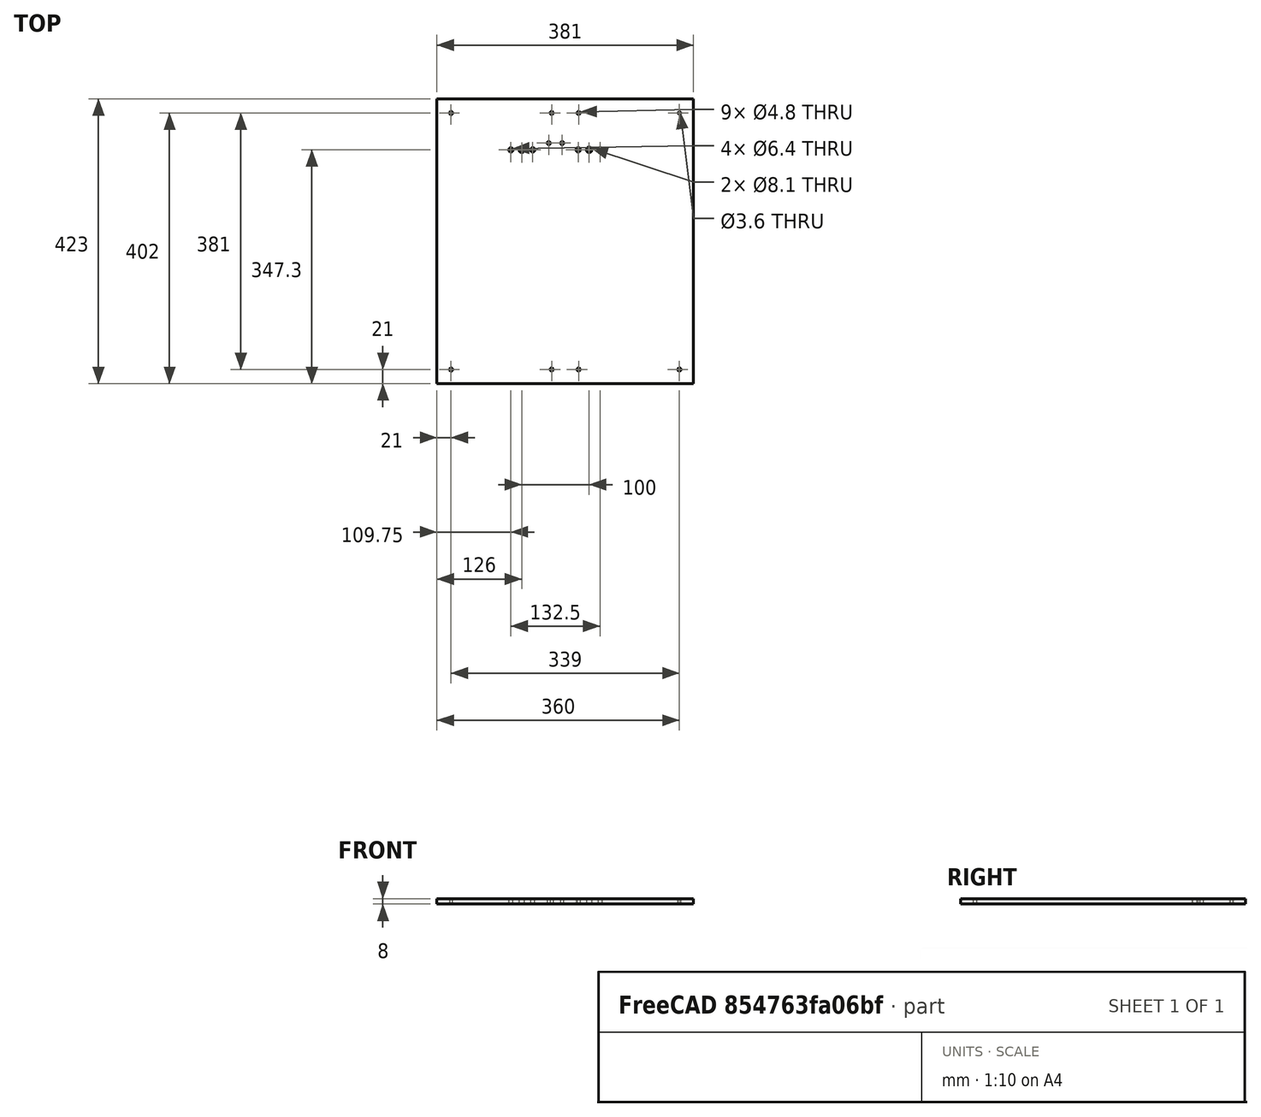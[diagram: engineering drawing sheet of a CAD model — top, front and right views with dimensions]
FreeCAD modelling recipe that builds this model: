
FCSTD DOCUMENT  (FreeCAD 0.16R6706 (Git))
Label: Piso
License: All rights reserved
LicenseURL: http://en.wikipedia.org/wiki/All_rights_reserved
objects: Path::FeaturePython×19, Sketcher::SketchObject×1, PartDesign::Pad×1, Path::FeatureCompoundPython×1
note: 3 computed .brp shape members not serialized (recipe doc carries the construction recipe); baked Part::Feature solids carry a one-line shape summary decoded from their .brp

FEATURE [Sketcher::SketchObject] Sketch
  sketch-geometry (29):
    g0: LineSegment StartX=-381 StartY=423 StartZ=0 EndX=0 EndY=423 EndZ=0
    g1: LineSegment StartX=0 StartY=423 StartZ=0 EndX=0 EndY=0 EndZ=0
    g2: LineSegment StartX=0 StartY=0 StartZ=0 EndX=-381 EndY=0 EndZ=0
    g3: LineSegment StartX=-381 StartY=0 StartZ=0 EndX=-381 EndY=423 EndZ=0
    g4: Circle CenterX=-360 CenterY=402 CenterZ=0 NormalX=0 NormalY=0 NormalZ=1 Radius=2.4
    g5: Circle CenterX=-21 CenterY=402 CenterZ=0 NormalX=0 NormalY=0 NormalZ=1 Radius=1.8
    g6: LineSegment [constr] StartX=-360 StartY=402 StartZ=0 EndX=-21 EndY=402 EndZ=0
    g7: LineSegment [constr] StartX=-21 StartY=402 StartZ=0 EndX=-21 EndY=21 EndZ=0
    g8: LineSegment [constr] StartX=-21 StartY=21 StartZ=0 EndX=-360 EndY=21 EndZ=0
    g9: LineSegment [constr] StartX=-360 StartY=21 StartZ=0 EndX=-360 EndY=402 EndZ=0
    g10: Circle CenterX=-360 CenterY=21 CenterZ=0 NormalX=0 NormalY=0 NormalZ=1 Radius=2.4
    g11: Circle CenterX=-21 CenterY=21 CenterZ=0 NormalX=0 NormalY=0 NormalZ=1 Radius=2.4
    g12: LineSegment [constr] StartX=-171.25 StartY=347.3 StartZ=0 EndX=-138.75 EndY=347.3 EndZ=0
    g13: Circle CenterX=-171.25 CenterY=347.3 CenterZ=0 NormalX=0 NormalY=0 NormalZ=1 Radius=3.2
    g14: Circle CenterX=-138.75 CenterY=347.3 CenterZ=0 NormalX=0 NormalY=0 NormalZ=1 Radius=3.2
    g15: LineSegment [constr] StartX=-271.25 StartY=347.3 StartZ=0 EndX=-238.75 EndY=347.3 EndZ=0
    g16: Circle CenterX=-271.25 CenterY=347.3 CenterZ=0 NormalX=0 NormalY=0 NormalZ=1 Radius=3.2
    g17: Circle CenterX=-238.75 CenterY=347.3 CenterZ=0 NormalX=0 NormalY=0 NormalZ=1 Radius=3.2
    g18: LineSegment [constr] StartX=-255 StartY=347.3 StartZ=0 EndX=-155 EndY=347.3 EndZ=0
    g19: LineSegment [constr] StartX=-205 StartY=347.3 StartZ=0 EndX=-205 EndY=327.3 EndZ=0
    g20: LineSegment [constr] StartX=-215 StartY=357.3 StartZ=0 EndX=-195 EndY=357.3 EndZ=0
    g21: Circle CenterX=-215 CenterY=357.3 CenterZ=0 NormalX=0 NormalY=0 NormalZ=1 Radius=2.4
    g22: Circle CenterX=-195 CenterY=357.3 CenterZ=0 NormalX=0 NormalY=0 NormalZ=1 Radius=2.4
    g23: Circle CenterX=-210.5 CenterY=402 CenterZ=0 NormalX=0 NormalY=0 NormalZ=1 Radius=2.4
    g24: Circle CenterX=-170.5 CenterY=402 CenterZ=0 NormalX=0 NormalY=0 NormalZ=1 Radius=2.4
    g25: Circle CenterX=-210.5 CenterY=21 CenterZ=0 NormalX=0 NormalY=0 NormalZ=1 Radius=2.4
    g26: Circle CenterX=-170.5 CenterY=21 CenterZ=0 NormalX=0 NormalY=0 NormalZ=1 Radius=2.4
    g27: Circle CenterX=-255 CenterY=347.3 CenterZ=0 NormalX=0 NormalY=0 NormalZ=1 Radius=4.05
    g28: Circle CenterX=-155 CenterY=347.3 CenterZ=0 NormalX=0 NormalY=0 NormalZ=1 Radius=4.05
  constraints (76):
    c: Coincident(g0,g1)
    c: Coincident(g1,g2)
    c: Coincident(g2,g3)
    c: Coincident(g3,g0)
    c: Horizontal(g0)
    c: Horizontal(g2)
    c: Vertical(g1)
    c: Vertical(g3)
    c: DistanceX(g0,g0) = 381
    c: DistanceY(g1,g1) = 423
    c: Coincident(g-1,g1)
    c: Radius(g4) = 2.4
    c: Coincident(g6,g7)
    c: Coincident(g7,g8)
    c: Coincident(g8,g9)
    c: Coincident(g9,g6)
    c: Horizontal(g6)
    c: Horizontal(g8)
    c: Vertical(g7)
    c: Vertical(g9)
    c: DistanceY(g-1,g7) = 21
    c: DistanceX(g7,g-1) = 21
    c: DistanceX(g0,g6) = 21
    c: DistanceY(g6,g0) = 21
    c: Equal(g4,g10) = 1.8
    c: Equal(g4,g11) = 1.8
    c: Coincident(g4,g6)
    c: Coincident(g5,g6)
    c: Coincident(g7,g11)
    c: Coincident(g8,g10)
    c: DistanceX(g12,g12) = 32.5
    c: Horizontal(g12)
    c: Radius(g13) = 3.2
    c: Equal(g13,g14) = 3.2
    c: Coincident(g12,g14)
    c: Coincident(g12,g13)
    c: Equal(g12,g15) = 32.5
    c: Horizontal(g15)
    c: Equal(g13,g16) = 3.2
    c: Equal(g16,g17) = 3.2
    c: Coincident(g15,g17)
    c: Coincident(g15,g16)
    c: DistanceX(g18,g18) = 100
    c: DistanceY(g19,g19) = 20
    c: Symmetric(g18,g18,g19)
    c: Horizontal(g18)
    c: Vertical(g19)
    c: Symmetric(g15,g15,g18)
    c: Symmetric(g12,g12,g18)
    c: DistanceX(g19,g0) = 205
    c: Horizontal(g20)
    c: DistanceX(g20,g20) = 20
    c: DistanceY(g19,g20) = 30
    c: Symmetric(g20,g20,g19)
    c: Equal(g4,g21) = 1.8
    c: Equal(g4,g22) = 1.8
    c: Coincident(g20,g21)
    c: Coincident(g22,g20)
    c: DistanceY(g12,g0) = 75.7
    c: DistanceX(g6,g6) = 339
    c: Radius(g23) = 2.4
    c: PointOnObject(g23,g6)
    c: DistanceX(g4,g23) = 149.5
    c: Equal(g23,g24) = 2.4
    c: PointOnObject(g24,g6)
    c: DistanceX(g23,g24) = 40
    c: Equal(g23,g25) = 2.4
    c: PointOnObject(g25,g8)
    c: DistanceX(g8,g25) = 149.5
    c: Equal(g23,g26) = 2.4
    c: PointOnObject(g26,g8)
    c: DistanceX(g25,g26) = 40
    c: Radius(g27) = 4.05
    c: Equal(g27,g28) = 4.05
    c: Coincident(g18,g28)
    c: Coincident(g18,g27)
FEATURE [PartDesign::Pad] Pad
  Length = 8
  Length2 = 100
  Sketch = -> Sketch
  Type = 0
FEATURE [Path::FeaturePython] Machine  label="Machine_"  # Path/CAM operation (typed FeaturePython)
  MachineUnits = 0
  X = 0
  X_Max = 0
  X_Min = 0
  Y = 0
  Y_Max = 0
  Y_Min = 0
  Z = 0
  Z_Max = 0
  Z_Min = 0
FEATURE [Path::FeaturePython] Tool  label="Tool1"  # Path/CAM operation (typed FeaturePython)
  SpindleDir = 0
  SpindleSpeed = 0
  ToolNumber = 1
FEATURE [Path::FeaturePython] Profile  label="Cantoneira"  # Path/CAM operation (typed FeaturePython)
  Active = true
  Base = -> Sketch
  ClearanceHeight = 3
  Direction = 1
  Edge1 = -> Sketch [Edge5]
  EndPoint = (0,0,0)
  ExtendAtEnd = 0
  ExtendAtStart = 0
  FinalDepth = -15.2
  HorizFeed = 127
  LeadInLineLen = 0
  LeadOutLineLen = 0
  OffsetExtra = 0
  PathClosed = true
  RetractHeight = 0
  RollRadius = 0
  SegLen = 0.5
  Side = 1
  StartDepth = 0
  StartPoint = (0,0,0)
  StepDown = 3
  ToolNumber = 1
  UseEndPoint = false
  UsePlacements = false
  UseStartDepth = true
  UseStartPoint = false
  VertFeed = 127
FEATURE [Path::FeaturePython] Profile001  label="Cantoneira001"  # Path/CAM operation (typed FeaturePython)
  Active = true
  Base = -> Sketch
  ClearanceHeight = 3
  Direction = 1
  Edge1 = -> Sketch [Edge15]
  EndPoint = (0,0,0)
  ExtendAtEnd = 0
  ExtendAtStart = 0
  FinalDepth = -15.2
  HorizFeed = 127
  LeadInLineLen = 0
  LeadOutLineLen = 0
  OffsetExtra = 0
  PathClosed = true
  RetractHeight = 0
  RollRadius = 0
  SegLen = 0.5
  Side = 1
  StartDepth = 0
  StartPoint = (0,0,0)
  StepDown = 3
  ToolNumber = 1
  UseEndPoint = false
  UsePlacements = false
  UseStartDepth = true
  UseStartPoint = false
  VertFeed = 127
FEATURE [Path::FeaturePython] Profile002  label="Cantoneira002"  # Path/CAM operation (typed FeaturePython)
  Active = true
  Base = -> Sketch
  ClearanceHeight = 3
  Direction = 1
  Edge1 = -> Sketch [Edge16]
  EndPoint = (0,0,0)
  ExtendAtEnd = 0
  ExtendAtStart = 0
  FinalDepth = -15.2
  HorizFeed = 127
  LeadInLineLen = 0
  LeadOutLineLen = 0
  OffsetExtra = 0
  PathClosed = true
  RetractHeight = 0
  RollRadius = 0
  SegLen = 0.5
  Side = 1
  StartDepth = 0
  StartPoint = (0,0,0)
  StepDown = 3
  ToolNumber = 1
  UseEndPoint = false
  UsePlacements = false
  UseStartDepth = true
  UseStartPoint = false
  VertFeed = 127
FEATURE [Path::FeaturePython] Profile003  label="Cantoneira003"  # Path/CAM operation (typed FeaturePython)
  Active = true
  Base = -> Sketch
  ClearanceHeight = 3
  Direction = 1
  Edge1 = -> Sketch [Edge6]
  EndPoint = (0,0,0)
  ExtendAtEnd = 0
  ExtendAtStart = 0
  FinalDepth = -15.2
  HorizFeed = 127
  LeadInLineLen = 0
  LeadOutLineLen = 0
  OffsetExtra = 0
  PathClosed = true
  RetractHeight = 0
  RollRadius = 0
  SegLen = 0.5
  Side = 1
  StartDepth = 0
  StartPoint = (0,0,0)
  StepDown = 3
  ToolNumber = 1
  UseEndPoint = false
  UsePlacements = false
  UseStartDepth = true
  UseStartPoint = false
  VertFeed = 127
FEATURE [Path::FeaturePython] Profile004  label="Cantoneira004"  # Path/CAM operation (typed FeaturePython)
  Active = true
  Base = -> Sketch
  ClearanceHeight = 3
  Direction = 1
  Edge1 = -> Sketch [Edge7]
  EndPoint = (0,0,0)
  ExtendAtEnd = 0
  ExtendAtStart = 0
  FinalDepth = -15.2
  HorizFeed = 127
  LeadInLineLen = 0
  LeadOutLineLen = 0
  OffsetExtra = 0
  PathClosed = true
  RetractHeight = 0
  RollRadius = 0
  SegLen = 0.5
  Side = 1
  StartDepth = 0
  StartPoint = (0,0,0)
  StepDown = 3
  ToolNumber = 1
  UseEndPoint = false
  UsePlacements = false
  UseStartDepth = true
  UseStartPoint = false
  VertFeed = 127
FEATURE [Path::FeaturePython] Profile005  label="Cantoneira005"  # Path/CAM operation (typed FeaturePython)
  Active = true
  Base = -> Sketch
  ClearanceHeight = 3
  Direction = 1
  Edge1 = -> Sketch [Edge17]
  EndPoint = (0,0,0)
  ExtendAtEnd = 0
  ExtendAtStart = 0
  FinalDepth = -15.2
  HorizFeed = 127
  LeadInLineLen = 0
  LeadOutLineLen = 0
  OffsetExtra = 0
  PathClosed = true
  RetractHeight = 0
  RollRadius = 0
  SegLen = 0.5
  Side = 1
  StartDepth = 0
  StartPoint = (0,0,0)
  StepDown = 3
  ToolNumber = 1
  UseEndPoint = false
  UsePlacements = false
  UseStartDepth = true
  UseStartPoint = false
  VertFeed = 127
FEATURE [Path::FeaturePython] Profile006  label="Cantoneira006"  # Path/CAM operation (typed FeaturePython)
  Active = true
  Base = -> Sketch
  ClearanceHeight = 3
  Direction = 1
  Edge1 = -> Sketch [Edge18]
  EndPoint = (0,0,0)
  ExtendAtEnd = 0
  ExtendAtStart = 0
  FinalDepth = -15.2
  HorizFeed = 127
  LeadInLineLen = 0
  LeadOutLineLen = 0
  OffsetExtra = 0
  PathClosed = true
  RetractHeight = 0
  RollRadius = 0
  SegLen = 0.5
  Side = 1
  StartDepth = 0
  StartPoint = (0,0,0)
  StepDown = 3
  ToolNumber = 1
  UseEndPoint = false
  UsePlacements = false
  UseStartDepth = true
  UseStartPoint = false
  VertFeed = 127
FEATURE [Path::FeaturePython] Profile007  label="Cantoneira007"  # Path/CAM operation (typed FeaturePython)
  Active = true
  Base = -> Sketch
  ClearanceHeight = 3
  Direction = 1
  Edge1 = -> Sketch [Edge8]
  EndPoint = (0,0,0)
  ExtendAtEnd = 0
  ExtendAtStart = 0
  FinalDepth = -15.2
  HorizFeed = 127
  LeadInLineLen = 0
  LeadOutLineLen = 0
  OffsetExtra = 0
  PathClosed = true
  RetractHeight = 0
  RollRadius = 0
  SegLen = 0.5
  Side = 1
  StartDepth = 0
  StartPoint = (0,0,0)
  StepDown = 3
  ToolNumber = 1
  UseEndPoint = false
  UsePlacements = false
  UseStartDepth = true
  UseStartPoint = false
  VertFeed = 127
FEATURE [Path::FeaturePython] Profile008  label="Motor e Haste"  # Path/CAM operation (typed FeaturePython)
  Active = true
  Base = -> Sketch
  ClearanceHeight = 3
  Direction = 1
  Edge1 = -> Sketch [Edge11]
  EndPoint = (0,0,0)
  ExtendAtEnd = 0
  ExtendAtStart = 0
  FinalDepth = -15.2
  HorizFeed = 127
  LeadInLineLen = 0
  LeadOutLineLen = 0
  OffsetExtra = 0
  PathClosed = true
  RetractHeight = 0
  RollRadius = 0
  SegLen = 0.5
  Side = 1
  StartDepth = 0
  StartPoint = (0,0,0)
  StepDown = 3
  ToolNumber = 1
  UseEndPoint = false
  UsePlacements = false
  UseStartDepth = true
  UseStartPoint = false
  VertFeed = 127
FEATURE [Path::FeaturePython] Profile009  label="Motor e Haste001"  # Path/CAM operation (typed FeaturePython)
  Active = true
  Base = -> Sketch
  ClearanceHeight = 3
  Direction = 1
  Edge1 = -> Sketch [Edge19]
  EndPoint = (0,0,0)
  ExtendAtEnd = 0
  ExtendAtStart = 0
  FinalDepth = -15.2
  HorizFeed = 127
  LeadInLineLen = 0
  LeadOutLineLen = 0
  OffsetExtra = 0
  PathClosed = true
  RetractHeight = 0
  RollRadius = 0
  SegLen = 0.5
  Side = 1
  StartDepth = 0
  StartPoint = (0,0,0)
  StepDown = 3
  ToolNumber = 1
  UseEndPoint = false
  UsePlacements = false
  UseStartDepth = true
  UseStartPoint = false
  VertFeed = 127
FEATURE [Path::FeaturePython] Profile010  label="Motor e Haste002"  # Path/CAM operation (typed FeaturePython)
  Active = true
  Base = -> Sketch
  ClearanceHeight = 3
  Direction = 1
  Edge1 = -> Sketch [Edge12]
  EndPoint = (0,0,0)
  ExtendAtEnd = 0
  ExtendAtStart = 0
  FinalDepth = -15.2
  HorizFeed = 127
  LeadInLineLen = 0
  LeadOutLineLen = 0
  OffsetExtra = 0
  PathClosed = true
  RetractHeight = 0
  RollRadius = 0
  SegLen = 0.5
  Side = 1
  StartDepth = 0
  StartPoint = (0,0,0)
  StepDown = 3
  ToolNumber = 1
  UseEndPoint = false
  UsePlacements = false
  UseStartDepth = true
  UseStartPoint = false
  VertFeed = 127
FEATURE [Path::FeaturePython] Profile011  label="Motor e Haste003"  # Path/CAM operation (typed FeaturePython)
  Active = true
  Base = -> Sketch
  ClearanceHeight = 3
  Direction = 1
  Edge1 = -> Sketch [Edge13]
  EndPoint = (0,0,0)
  ExtendAtEnd = 0
  ExtendAtStart = 0
  FinalDepth = -15.2
  HorizFeed = 127
  LeadInLineLen = 0
  LeadOutLineLen = 0
  OffsetExtra = 0
  PathClosed = true
  RetractHeight = 0
  RollRadius = 0
  SegLen = 0.5
  Side = 1
  StartDepth = 0
  StartPoint = (0,0,0)
  StepDown = 3
  ToolNumber = 1
  UseEndPoint = false
  UsePlacements = false
  UseStartDepth = true
  UseStartPoint = false
  VertFeed = 127
FEATURE [Path::FeaturePython] Profile012  label="Motor e Haste004"  # Path/CAM operation (typed FeaturePython)
  Active = true
  Base = -> Sketch
  ClearanceHeight = 3
  Direction = 1
  Edge1 = -> Sketch [Edge14]
  EndPoint = (0,0,0)
  ExtendAtEnd = 0
  ExtendAtStart = 0
  FinalDepth = -15.2
  HorizFeed = 127
  LeadInLineLen = 0
  LeadOutLineLen = 0
  OffsetExtra = 0
  PathClosed = true
  RetractHeight = 0
  RollRadius = 0
  SegLen = 0.5
  Side = 1
  StartDepth = 0
  StartPoint = (0,0,0)
  StepDown = 3
  ToolNumber = 1
  UseEndPoint = false
  UsePlacements = false
  UseStartDepth = true
  UseStartPoint = false
  VertFeed = 127
FEATURE [Path::FeaturePython] Profile013  label="Motor e Haste005"  # Path/CAM operation (typed FeaturePython)
  Active = true
  Base = -> Sketch
  ClearanceHeight = 3
  Direction = 1
  Edge1 = -> Sketch [Edge9]
  EndPoint = (0,0,0)
  ExtendAtEnd = 0
  ExtendAtStart = 0
  FinalDepth = -15.2
  HorizFeed = 127
  LeadInLineLen = 0
  LeadOutLineLen = 0
  OffsetExtra = 0
  PathClosed = true
  RetractHeight = 0
  RollRadius = 0
  SegLen = 0.5
  Side = 1
  StartDepth = 0
  StartPoint = (0,0,0)
  StepDown = 3
  ToolNumber = 1
  UseEndPoint = false
  UsePlacements = false
  UseStartDepth = true
  UseStartPoint = false
  VertFeed = 127
FEATURE [Path::FeaturePython] Profile014  label="Motor e Haste006"  # Path/CAM operation (typed FeaturePython)
  Active = true
  Base = -> Sketch
  ClearanceHeight = 3
  Direction = 1
  Edge1 = -> Sketch [Edge20]
  EndPoint = (0,0,0)
  ExtendAtEnd = 0
  ExtendAtStart = 0
  FinalDepth = -15.2
  HorizFeed = 127
  LeadInLineLen = 0
  LeadOutLineLen = 0
  OffsetExtra = 0
  PathClosed = true
  RetractHeight = 0
  RollRadius = 0
  SegLen = 0.5
  Side = 1
  StartDepth = 0
  StartPoint = (0,0,0)
  StepDown = 3
  ToolNumber = 1
  UseEndPoint = false
  UsePlacements = false
  UseStartDepth = true
  UseStartPoint = false
  VertFeed = 127
FEATURE [Path::FeaturePython] Profile015  label="Motor e Haste007"  # Path/CAM operation (typed FeaturePython)
  Active = true
  Base = -> Sketch
  ClearanceHeight = 3
  Direction = 1
  Edge1 = -> Sketch [Edge10]
  EndPoint = (0,0,0)
  ExtendAtEnd = 0
  ExtendAtStart = 0
  FinalDepth = -15.2
  HorizFeed = 127
  LeadInLineLen = 0
  LeadOutLineLen = 0
  OffsetExtra = 0
  PathClosed = true
  RetractHeight = 0
  RollRadius = 0
  SegLen = 0.5
  Side = 1
  StartDepth = 0
  StartPoint = (0,0,0)
  StepDown = 3
  ToolNumber = 1
  UseEndPoint = false
  UsePlacements = false
  UseStartDepth = true
  UseStartPoint = false
  VertFeed = 127
FEATURE [Path::FeaturePython] Profile016  label="Externo"  # Path/CAM operation (typed FeaturePython)
  Active = true
  Base = -> Sketch
  ClearanceHeight = 3
  Direction = 0
  Edge1 = -> Sketch [Edge4]
  Edge2 = -> Sketch [Edge3]
  EndPoint = (0,0,0)
  ExtendAtEnd = 0
  ExtendAtStart = 0
  FinalDepth = -15.2
  HorizFeed = 127
  LeadInLineLen = 0
  LeadOutLineLen = 0
  OffsetExtra = 0
  PathClosed = true
  RetractHeight = 0
  RollRadius = 0
  SegLen = 0.5
  Side = 0
  StartDepth = 0
  StartPoint = (0,0,0)
  StepDown = 3
  ToolNumber = 1
  UseEndPoint = false
  UsePlacements = false
  UseStartDepth = true
  UseStartPoint = false
  VertFeed = 127
FEATURE [Path::FeatureCompoundPython] Project  # Path/CAM operation (typed FeaturePython)
  Group = -> [Machine,Tool,Profile,Profile001,Profile002,Profile003,Profile004,Profile005,Profile006,Profile007,Profile008,Profile009,Profile010,Profile011,Profile012,Profile013,Profile014,Profile015,Profile016]
  UsePlacements = false
